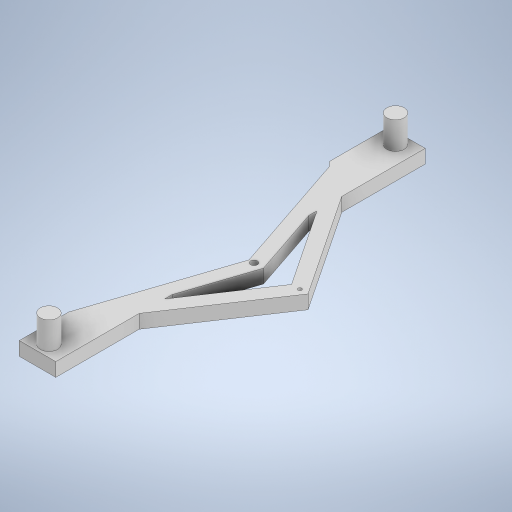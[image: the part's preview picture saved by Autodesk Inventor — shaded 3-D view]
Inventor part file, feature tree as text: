
AUTODESK INVENTOR PART (.ipt)
format: ipt  version: 2024 (Build 280153000, 153)  size: 333,824 bytes
history: native  units: in
note: dims shown in document units (in); Inventor stores cm internally (conversion verified against a paired STEP export)
features: extrude x8, sketch x6, chamfer x1, fillet x1
ambient origin geometry x8: Origin, YZ Plane, XZ Plane, XY Plane, X Axis, Y Axis, Z Axis, Center Point
bodies: Solid1 (feature_tree)
feature tree (16):
  sketch  "Sketch1"  dims[d0=3.189in d1=0.315in]
  extrude  "Extrusion1"  Depth=0.315in
  extrude  "Extrusion2"  Depth=3.189in
  sketch  "Sketch2"  dims[d2=3.189in d3=0.0984in]
  extrude  "Extrusion3"  Depth=0.1496in
  extrude  "Extrusion4"  Depth=0.1181in TaperAngle=0.0deg
  chamfer  "Chamfer1"  Distance=0.3543in
  fillet  "Fillet1"  Radius=0.3937in
  extrude  "Extrusion5"  Depth=0.5906in
  extrude  "Extrusion6"  Depth=0.0394in
  extrude  "Extrusion7"  Depth=0.1181in
  extrude  "Extrusion8"  Depth=0.1181in TaperAngle=0.0deg
  sketch  "Sketch3"  dims[d4=0.0984in d5=0.1496in]
  sketch  "Sketch4"  dims[d6=0.1496in d7=0.1181in d8=0.0in d9=0.3543in d10=0.0in d11=0.3937in]
  sketch  "Sketch5"  dims[d12=0.5906in d13=0.5906in]
  sketch  "Sketch6"  dims[d14=0.0394in d15=0.0394in d16=0.1181in d17=0.1181in d18=0.0in d19=0.1181in d20=0.0in d21=0.1181in d22=0.0787in d23=45.0deg d24=0.0394in d25=0.071in d26=0.0315in d27=0.1181in d28=0.0in d29=0.315in d30=0.1181in d31=0.0591in d32=0.1181in d33=0.0in d34=0.1181in d35=0.0in d36=0.0726in d37=0.0435in d38=0.1181in d39=0.0in]
